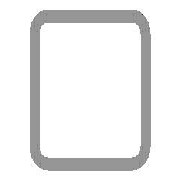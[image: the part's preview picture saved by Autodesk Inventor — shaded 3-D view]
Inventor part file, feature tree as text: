
AUTODESK INVENTOR PART (.ipt)
format: ipt  version: 2025 (Build 290162010, 162A)  size: 167,424 bytes
history: native  units: mm (DEFAULTED — no unit token found)
features: other x3, sketch x3, projected_geometry x2, extrude x1, plane x1
ambient origin geometry x8: Origin, YZ Plane, XZ Plane, XY Plane, X Axis, Y Axis, Z Axis, Center Point
bodies: Solid1 (feature_tree), Body (feature_tree)
feature tree (10):
  other  "Driven Length"
  other  "Start plane"
  other  "End plane"
  sketch  "Sketch5"  dims[d7=6.0mm]
  extrude  "Extrusion2"  TaperAngle=0.0deg  [1 undecoded]
  sketch  "Sketch3"  dims[d3=1000.0mm d4=0.0mm]
  plane  "Work Plane3"
  sketch  "Sketch6"  dims[d9=80.0mm d11=80.0mm d12=3.0mm d13=-0.0mm d14=1000.0mm d15=40.0mm d16=40.0mm d17=90.0deg d18=1000.0mm d22=300.0mm d24=940.0mm d25=89.3mm d26=40.0mm d27=940.0mm d28=300.0mm d30=349.157702mm d31=0.0mm d32=0.0mm d33=10.0mm]
  projected_geometry  "Projected Loop1"
  projected_geometry  "Projected Loop2"
note: 1 required parameter value undecoded (feature->parameter linkage not recoverable at this tier; creation-order binding heuristic only, values carry confidence <= 0.55)
